# Revit family: Shinhoo_Basic_F
name_source: partatom
category: Оборудование
units: mm (PartAtom-declared; Revit-internal decimal feet)

## family parameters
Всегда вертикально = Нет
Классификация = Нет
На основе рабочей плоскости = Нет
Общий = Нет
При загрузке вырезать с полостями = Нет
Размер круглого соединителя = Использовать диаметр
Тип детали = Вставляется
Точка расчета площади = Нет

## types (17) — shared parameters
ADSK_URL страницы изделия = https://shinhoopump.ru
ADSK_Версия Revit = 2019
ADSK_Версия семейства = 1.0
ADSK_Единица измерения = шт
ADSK_Завод-изготовитель = Shinhoo
ADSK_Количество = 1
ADSK_Коэффициент мощности = 1
ADSK_Материал = Чугун с катафорезным покрытием
ADSK_Обозначение = ГОСТ 31839-2012, ГОСТ 12.2.007.0-75, ГОСТ 12.2.003-91, ГОСТ Р МЭК 60204-1-2007,  ГОСТ 30804
URL = https://shinhoopump.ru
Изготовитель = Shinhoo
Класс защиты (IP) = IP44
Разработчик = ООО ПРОРУБИМ
Разработчик (телефон) = +7(495)649-85-43
Скорость вращения = 2850
Степень защиты от удара (IK) = IK04
Тип Насоса = Стандартный циркуляционный насос с «мокрым» ротором
Тип основания = встроенный

## per-type parameters (varying)
- BASIC 32-8SF 200 1x230В - 71221001: ADSK_Код изделия=71221001; ADSK_Масса=5.8; ADSK_Масса_Текст=5.8; ADSK_Наименование=Стандартный циркуляционный насос с «мокрым» ротором BASIC 32-8SF 200 1x230В; ADSK_Наименование краткое=BASIC 32-8SF 200 1x230В; ADSK_Напряжение=230 В; ADSK_Номинальная мощность=245 Вт; ADSK_Полная мощность=245 В·А; ADSK_Расход жидкости=0.002222 м³/с; ADSK_Ток=1 А; B=150 мм; B1=58 мм; B2=92 мм; D1=40 мм; D6=90 мм; DN=32 мм; H=185 мм; H1=130 мм; H2=55 мм; L=200 мм; b1_10=46 мм; b1_20=39 мм; r1=20 мм; r1_1=21 мм; r1_3=30 мм; r6=45 мм; Группа модели=BASIC 32-8SF
- BASIC 32-12F 220 1x230В - 71221002: ADSK_Код изделия=71221002; ADSK_Масса=9.3; ADSK_Масса_Текст=9.3; ADSK_Наименование=Стандартный циркуляционный насос с «мокрым» ротором; ADSK_Наименование краткое=BASIC 32-12F 1x230V; ADSK_Напряжение=230 В; ADSK_Номинальная мощность=500 Вт; ADSK_Полная мощность=500 В·А; ADSK_Расход жидкости=0.002778 м³/с; ADSK_Ток=3 А; B=167 мм; B1=68 мм; B2=99 мм; D1=40 мм; D6=90 мм; DN=32 мм; H=234 мм; H1=185 мм; H2=49 мм; L=220 мм; b1_10=54 мм; b1_20=45 мм; r1=20 мм; r1_1=21 мм; r1_3=30 мм; r6=45 мм; Группа модели=BASIC 32-12F
- BASIC 40-12F 250 1x230В - 71221003: ADSK_Код изделия=71221003; ADSK_Масса=15.3; ADSK_Масса_Текст=15.3; ADSK_Наименование=Стандартный циркуляционный насос с «мокрым» ротором BASIC 40-12F 250 1x230В; ADSK_Наименование краткое=BASIC 40-12F 250 1x230В; ADSK_Напряжение=230 В; ADSK_Номинальная мощность=700 Вт; ADSK_Полная мощность=700 В·А; ADSK_Расход жидкости=0.003333 м³/с; ADSK_Ток=3 А; B=234 мм; B1=80 мм; B2=154 мм; D1=40 мм; D6=150 мм; DN=40 мм; H=297 мм; H1=232 мм; H2=65 мм; L=250 мм; b1_10=64 мм; b1_20=53 мм; r1=20 мм; r1_1=21 мм; r1_3=30 мм; r6=75 мм; Группа модели=BASIC 40-12F
- BASIC 40-12SF 250 3x380В - 71222001: ADSK_Код изделия=71222001; ADSK_Масса=15.3; ADSK_Масса_Текст=15.3; ADSK_Наименование=Стандартный циркуляционный насос с «мокрым» ротором BASIC 40-12SF 250 3x380В; ADSK_Наименование краткое=BASIC 40-12SF 250 3x380В; ADSK_Напряжение=380 В; ADSK_Номинальная мощность=700 Вт; ADSK_Полная мощность=700 В·А; ADSK_Расход жидкости=0.003889 м³/с; ADSK_Ток=1 А; B=234 мм; B1=80 мм; B2=154 мм; D1=40 мм; D6=150 мм; DN=40 мм; H=297 мм; H1=232 мм; H2=65 мм; L=250 мм; b1_10=64 мм; b1_20=53 мм; r1=20 мм; r1_1=21 мм; r1_3=30 мм; r6=75 мм; Группа модели=BASIC 40-12SF
- BASIC 40-16F 250 1x230В - 71221004: ADSK_Код изделия=71221004; ADSK_Масса=16.9; ADSK_Масса_Текст=16.9; ADSK_Наименование=Стандартный циркуляционный насос с «мокрым» ротором BASIC 40-16F 250 1x230В; ADSK_Наименование краткое=BASIC 40-16F 250 1x230В; ADSK_Напряжение=230 В; ADSK_Номинальная мощность=1000 Вт; ADSK_Полная мощность=1000 В·А; ADSK_Расход жидкости=0.003750 м³/с; ADSK_Ток=5 А; B=234 мм; B1=80 мм; B2=154 мм; D1=40 мм; D6=150 мм; DN=40 мм; H=297 мм; H1=232 мм; H2=65 мм; L=250 мм; b1_10=64 мм; b1_20=53 мм; r1=20 мм; r1_1=21 мм; r1_3=30 мм; r6=75 мм; Группа модели=BASIC 40-16F
- BASIC 40-16SF 250 3x380В - 71222002: ADSK_Код изделия=71222002; ADSK_Масса=16.9; ADSK_Масса_Текст=16.9; ADSK_Наименование=Стандартный циркуляционный насос с «мокрым» ротором BASIC 40-16SF 250 3x380В; ADSK_Наименование краткое=BASIC 40-16SF 250 3x380В; ADSK_Напряжение=380 В; ADSK_Номинальная мощность=1000 Вт; ADSK_Полная мощность=1000 В·А; ADSK_Расход жидкости=0.004583 м³/с; ADSK_Ток=2 А; B=234 мм; B1=80 мм; B2=154 мм; D1=40 мм; D6=150 мм; DN=40 мм; H=297 мм; H1=232 мм; H2=65 мм; L=250 мм; b1_10=64 мм; b1_20=53 мм; r1=20 мм; r1_1=21 мм; r1_3=30 мм; r6=75 мм; Группа модели=BASIC 40-16SF
- BASIC 50-12F 280 1x230В - 71221005: ADSK_Код изделия=71221005; ADSK_Масса=17.6; ADSK_Масса_Текст=17.6; ADSK_Наименование=Стандартный циркуляционный насос с «мокрым» ротором BASIC 50-12F 280 1x230В; ADSK_Наименование краткое=BASIC 50-12F 280 1x230В; ADSK_Напряжение=230 В; ADSK_Номинальная мощность=1000 Вт; ADSK_Полная мощность=1000 В·А; ADSK_Расход жидкости=0.007222 м³/с; ADSK_Ток=5 А; B=242 мм; B1=88 мм; B2=154 мм; D1=50 мм; D6=165 мм; DN=50 мм; H=304 мм; H1=232 мм; H2=72 мм; L=280 мм; b1_10=70 мм; b1_20=59 мм; r1=25 мм; r1_1=26 мм; r1_3=38 мм; r6=83 мм; Группа модели=BASIC 50-12F
- BASIC 50-12SF 280 3x380В - 71222003: ADSK_Код изделия=71222003; ADSK_Масса=17.5; ADSK_Масса_Текст=17.5; ADSK_Наименование=Стандартный циркуляционный насос с «мокрым» ротором BASIC 50-12SF 280 3x380В; ADSK_Наименование краткое=BASIC 50-12SF 280 3x380В; ADSK_Напряжение=380 В; ADSK_Номинальная мощность=1000 Вт; ADSK_Полная мощность=1000 В·А; ADSK_Расход жидкости=0.006667 м³/с; ADSK_Ток=2 А; B=242 мм; B1=88 мм; B2=154 мм; D1=50 мм; D6=165 мм; DN=50 мм; H=304 мм; H1=232 мм; H2=72 мм; L=280 мм; b1_10=70 мм; b1_20=59 мм; r1=25 мм; r1_1=26 мм; r1_3=38 мм; r6=83 мм; Группа модели=BASIC 50-12SF
- BASIC 50-16F 280 1x230В - 71221006: ADSK_Код изделия=71221006; ADSK_Масса=19.6; ADSK_Масса_Текст=19.6; ADSK_Наименование=Стандартный циркуляционный насос с «мокрым» ротором BASIC 50-16F 280 1x230В; ADSK_Наименование краткое=BASIC 50-16F 280 1x230В; ADSK_Напряжение=230 В; ADSK_Номинальная мощность=1300 Вт; ADSK_Полная мощность=1300 В·А; ADSK_Расход жидкости=0.007222 м³/с; ADSK_Ток=6 А; B=242 мм; B1=88 мм; B2=154 мм; D1=50 мм; D6=165 мм; DN=50 мм; H=329 мм; H1=257 мм; H2=72 мм; L=280 мм; b1_10=70 мм; b1_20=59 мм; r1=25 мм; r1_1=26 мм; r1_3=38 мм; r6=83 мм; Группа модели=BASIC 50-16F
- BASIC 50-16SF 280 3x380В - 71222004: ADSK_Код изделия=71222004; ADSK_Масса=19.6; ADSK_Масса_Текст=19.6; ADSK_Наименование=Стандартный циркуляционный насос с «мокрым» ротором BASIC 50-16SF 280 3x380В; ADSK_Наименование краткое=BASIC 50-16SF 280 3x380В; ADSK_Напряжение=380 В; ADSK_Номинальная мощность=1300 Вт; ADSK_Полная мощность=1300 В·А; ADSK_Расход жидкости=0.007778 м³/с; ADSK_Ток=3 А; B=242 мм; B1=88 мм; B2=154 мм; D1=50 мм; D6=165 мм; DN=50 мм; H=329 мм; H1=257 мм; H2=72 мм; L=280 мм; b1_10=70 мм; b1_20=59 мм; r1=25 мм; r1_1=26 мм; r1_3=38 мм; r6=83 мм; Группа модели=BASIC 50-16SF
- BASIC 50-20F 280 1x230В - 71221007: ADSK_Код изделия=71221007; ADSK_Масса=19.8; ADSK_Масса_Текст=19.8; ADSK_Наименование=Стандартный циркуляционный насос с «мокрым» ротором BASIC 50-20F 280 1x230В; ADSK_Наименование краткое=BASIC 50-20F 280 1x230В; ADSK_Напряжение=230 В; ADSK_Номинальная мощность=1300 Вт; ADSK_Полная мощность=1300 В·А; ADSK_Расход жидкости=0.005833 м³/с; ADSK_Ток=6 А; B=242 мм; B1=88 мм; B2=154 мм; D1=50 мм; D6=165 мм; DN=50 мм; H=329 мм; H1=257 мм; H2=72 мм; L=280 мм; b1_10=70 мм; b1_20=59 мм; r1=25 мм; r1_1=26 мм; r1_3=38 мм; r6=83 мм; Группа модели=BASIC 50-20F
- BASIC 50-20SF 280 3x380В - 71222005: ADSK_Код изделия=71222005; ADSK_Масса=19.8; ADSK_Масса_Текст=19.8; ADSK_Наименование=Стандартный циркуляционный насос с «мокрым» ротором BASIC 50-20SF 280 3x380В; ADSK_Наименование краткое=BASIC 50-20SF 280 3x380В; ADSK_Напряжение=380 В; ADSK_Номинальная мощность=1300 Вт; ADSK_Полная мощность=1300 В·А; ADSK_Расход жидкости=0.006667 м³/с; ADSK_Ток=3 А; B=242 мм; B1=88 мм; B2=154 мм; D1=50 мм; D6=165 мм; DN=50 мм; H=329 мм; H1=257 мм; H2=72 мм; L=280 мм; b1_10=70 мм; b1_20=59 мм; r1=25 мм; r1_1=26 мм; r1_3=38 мм; r6=83 мм; Группа модели=BASIC 50-20SF
- BASIC 65-8F 280 1x230В - 71221008: ADSK_Код изделия=71221008; ADSK_Масса=18.2; ADSK_Масса_Текст=18.2; ADSK_Наименование=Стандартный циркуляционный насос с «мокрым» ротором BASIC 65-8F 280 1x230В; ADSK_Наименование краткое=BASIC 65-8F 280 1x230В; ADSK_Напряжение=230 В; ADSK_Номинальная мощность=700 Вт; ADSK_Полная мощность=700 В·А; ADSK_Расход жидкости=0.008333 м³/с; ADSK_Ток=3 А; B=242 мм; B1=88 мм; B2=154 мм; D1=65 мм; D6=185 мм; DN=65 мм; H=310 мм; H1=232 мм; H2=78 мм; L=280 мм; b1_10=70 мм; b1_20=59 мм; r1=33 мм; r1_1=34 мм; r1_3=49 мм; r6=93 мм; Группа модели=BASIC 65-8F
- BASIC 65-8SF 280 3x380В - 71222006: ADSK_Код изделия=71222006; ADSK_Масса=18.2; ADSK_Масса_Текст=18.2; ADSK_Наименование=Стандартный циркуляционный насос с «мокрым» ротором BASIC 65-8SF 280 3x380В; ADSK_Наименование краткое=BASIC 65-8SF 280 3x380В; ADSK_Напряжение=380 В; ADSK_Номинальная мощность=700 Вт; ADSK_Полная мощность=700 В·А; ADSK_Расход жидкости=0.009722 м³/с; ADSK_Ток=1 А; B=242 мм; B1=88 мм; B2=154 мм; D1=65 мм; D6=180 мм; DN=65 мм; H=310 мм; H1=232 мм; H2=78 мм; L=280 мм; b1_10=70 мм; b1_20=59 мм; r1=33 мм; r1_1=34 мм; r1_3=49 мм; r6=90 мм; Группа модели=BASIC 65-8SF
- BASIC 65-12F 300 1x230В - 71221009: ADSK_Код изделия=71221009; ADSK_Масса=21.5; ADSK_Масса_Текст=21.5; ADSK_Наименование=Стандартный циркуляционный насос с «мокрым» ротором BASIC 65-12F 300 1x230В; ADSK_Наименование краткое=BASIC 65-12F 300 1x230В; ADSK_Напряжение=230 В; ADSK_Номинальная мощность=1300 Вт; ADSK_Полная мощность=1300 В·А; ADSK_Расход жидкости=0.011111 м³/с; ADSK_Ток=6 А; B=247 мм; B1=93 мм; B2=154 мм; D1=65 мм; D6=185 мм; DN=65 мм; H=335 мм; H1=257 мм; H2=78 мм; L=300 мм; b1_10=74 мм; b1_20=62 мм; r1=33 мм; r1_1=34 мм; r1_3=49 мм; r6=93 мм; Группа модели=BASIC 65-12F
- BASIC 65-12SF 300 3x380В - 71222007: ADSK_Код изделия=71222007; ADSK_Масса=21.5; ADSK_Масса_Текст=21.5; ADSK_Наименование=Стандартный циркуляционный насос с «мокрым» ротором BASIC 65-12SF 300 3x380В; ADSK_Наименование краткое=BASIC 65-12SF 300 3x380В; ADSK_Напряжение=380 В; ADSK_Номинальная мощность=1300 Вт; ADSK_Полная мощность=1300 В·А; ADSK_Расход жидкости=0.013611 м³/с; ADSK_Ток=3 А; B=247 мм; B1=93 мм; B2=154 мм; D1=65 мм; D6=185 мм; DN=65 мм; H=335 мм; H1=257 мм; H2=78 мм; L=300 мм; b1_10=74 мм; b1_20=62 мм; r1=33 мм; r1_1=34 мм; r1_3=49 мм; r6=93 мм; Группа модели=BASIC 65-12SF
- BASIC 80-12SF 360 3x380В - 71222008: ADSK_Код изделия=71222008; ADSK_Масса=24.4; ADSK_Масса_Текст=24.4; ADSK_Наименование=Стандартный циркуляционный насос с «мокрым» ротором BASIC 80-12SF 360 3x380В; ADSK_Наименование краткое=BASIC 80-12SF 360 3x380В; ADSK_Напряжение=380 В; ADSK_Номинальная мощность=1300 Вт; ADSK_Полная мощность=1300 В·А; ADSK_Расход жидкости=0.010556 м³/с; ADSK_Ток=3 А; B=247 мм; B1=93 мм; B2=154 мм; D1=80 мм; D6=200 мм; DN=80 мм; H=345 мм; H1=257 мм; H2=88 мм; L=360 мм; b1_10=74 мм; b1_20=62 мм; r1=40 мм; r1_1=41 мм; r1_3=60 мм; r6=100 мм; Группа модели=BASIC 80-12SF

## geometry (parser evidence)
native form markers: Sweep x3
no freeform markers — native parametric forms only
